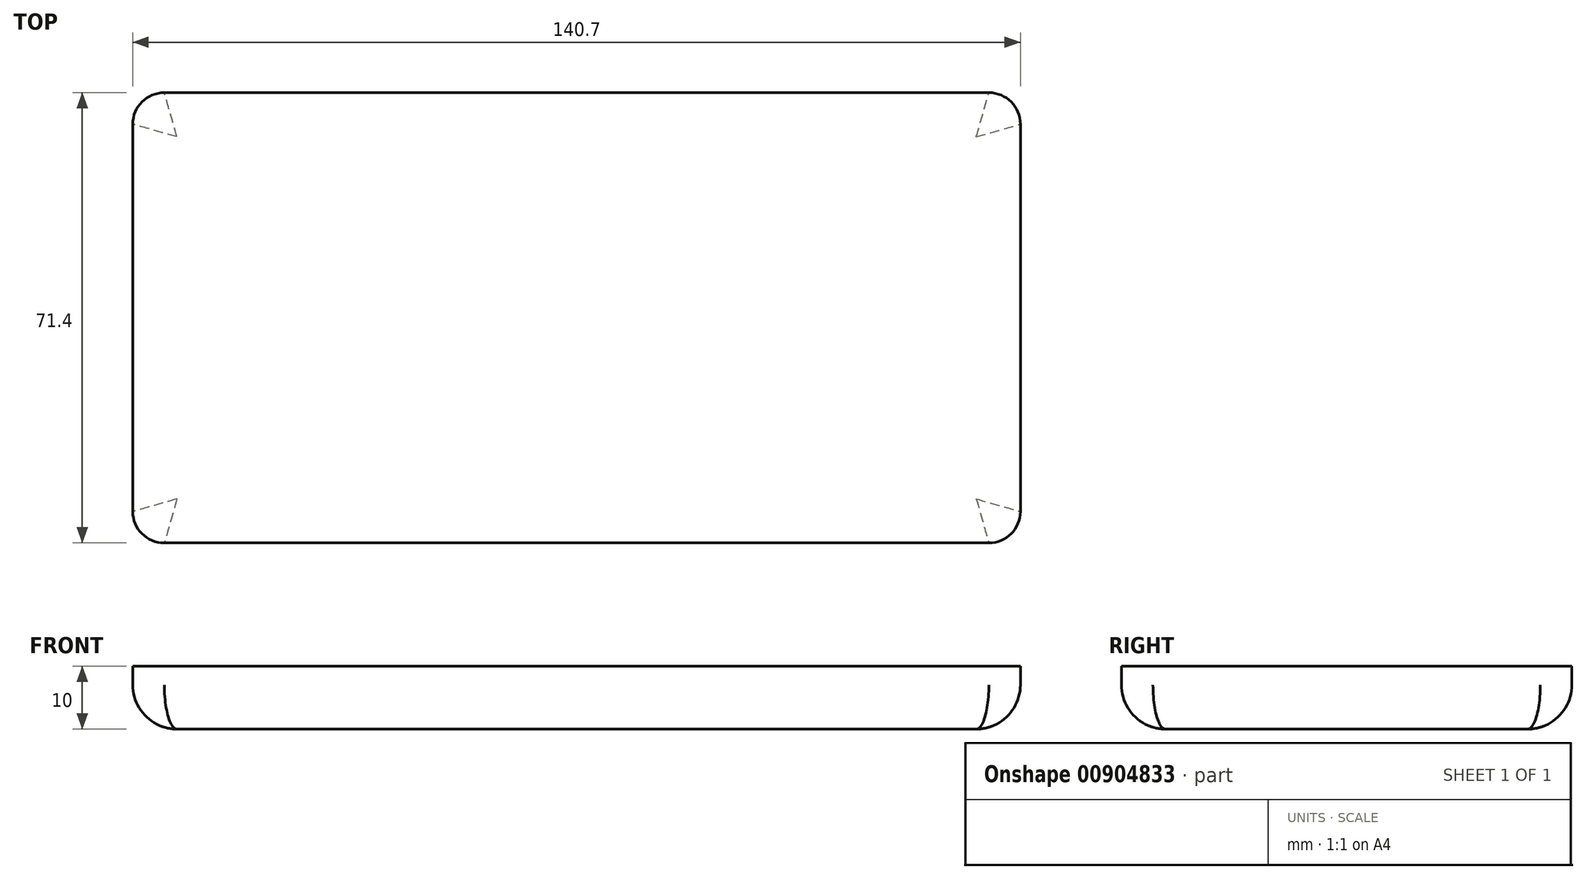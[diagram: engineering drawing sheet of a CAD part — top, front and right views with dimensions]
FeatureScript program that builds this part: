
annotation { "Feature Type Name" : "Feature", "Feature Type Description" : "" }
export const myFeature = defineFeature(function(context is Context, id is Id, definition is map)
    precondition{}
    {
        {
            var Q0;
            Q0=qCreatedBy(makeId("Top.planeOp"),FACE);
            var sketch = newSketch(context, id + "F0", { "sketchPlane" : qUnion([Q0])});
            skLineSegment(sketch, "E0.bottom", {"start": v(70.35, -35.7) * mm, "end": v(-70.35, -35.7) * mm});
            skLineSegment(sketch, "E0.top", {"start": v(70.35, 35.7) * mm, "end": v(-70.35, 35.7) * mm});
            skLineSegment(sketch, "E0.left", {"start": v(70.35, -35.7) * mm, "end": v(70.35, 35.7) * mm});
            skLineSegment(sketch, "E0.right", {"start": v(-70.35, -35.7) * mm, "end": v(-70.35, 35.7) * mm});
            skPoint(sketch, "E0.middle", {"position": v(0, 0) * mm});
            skSolve(sketch);
        }
        {
            var Q0;
            Q0 = qSketchRegion(id + "F0", true);
            extrude(context, id + "F1", {"entities" : qUnion([Q0]), "depth" : 10 * mm, "offsetDistance" : 25 * mm});
        }
        {
            var Q0;
            Q0=makeQuery(id+"F1.opExtrude","SWEPT_EDGE",EDGE,{"disambiguationData":[OSD([sQuery(id+"F0.wireOp",EDGE,"E0.bottom"),sQuery(id+"F0.wireOp",EDGE,"E0.left")])]});
            var Q1;
            Q1=makeQuery(id+"F1.opExtrude","SWEPT_EDGE",EDGE,{"disambiguationData":[OSD([sQuery(id+"F0.wireOp",EDGE,"E0.top"),sQuery(id+"F0.wireOp",EDGE,"E0.left")])]});
            var Q2;
            Q2=makeQuery(id+"F1.opExtrude","SWEPT_EDGE",EDGE,{"disambiguationData":[OSD([sQuery(id+"F0.wireOp",EDGE,"E0.top"),sQuery(id+"F0.wireOp",EDGE,"E0.right")])]});
            var Q3;
            Q3=makeQuery(id+"F1.opExtrude","SWEPT_EDGE",EDGE,{"disambiguationData":[OSD([sQuery(id+"F0.wireOp",EDGE,"E0.bottom"),sQuery(id+"F0.wireOp",EDGE,"E0.right")])]});
            fillet(context, id + "F2", {"entities" : qUnion([Q0, Q1, Q2, Q3]), "radius" : 5 * mm, "tangentPropagation" : true, "allowEdgeOverflow" : false});
        }
        {
            var Q0;
            Q0=makeQuery(id+"F1.opExtrude","CAP_FACE",FACE,{"disambiguationData":[OSD([sQuery(id+"F0.wireOp",EDGE,"E0.bottom"),sQuery(id+"F0.wireOp",EDGE,"E0.top"),sQuery(id+"F0.wireOp",EDGE,"E0.left"),sQuery(id+"F0.wireOp",EDGE,"E0.right")])],"isStart":true});
            fillet(context, id + "F3", {"entities" : qUnion([Q0]), "radius" : 7 * mm, "tangentPropagation" : true, "allowEdgeOverflow" : false});
        }
    });
